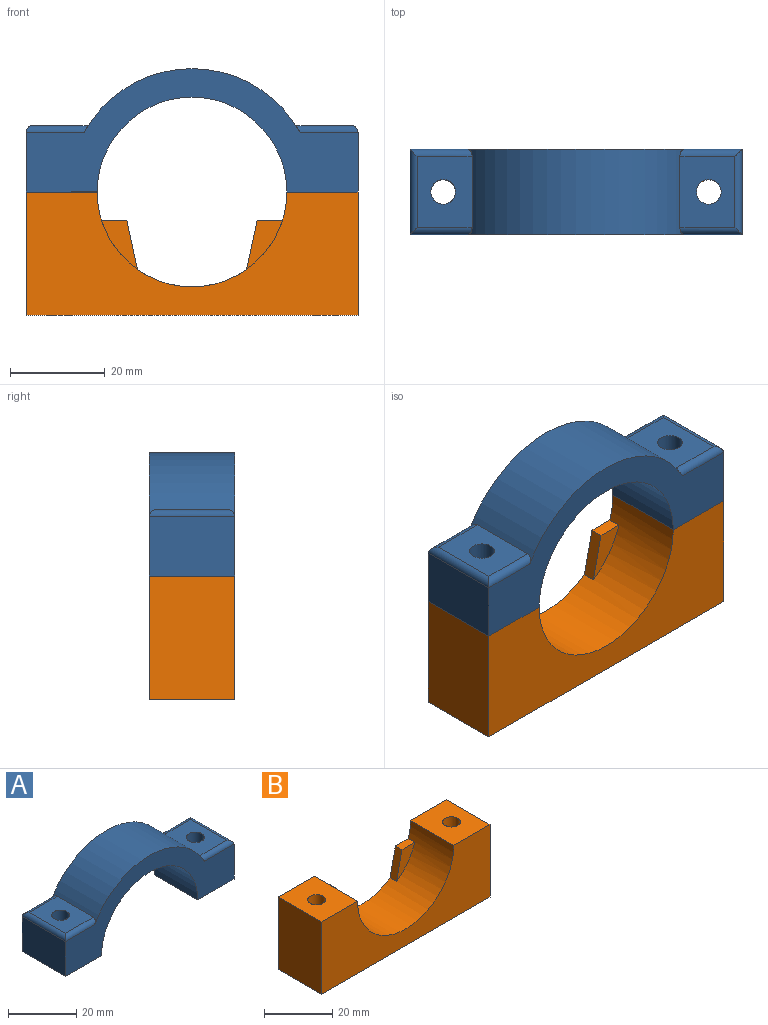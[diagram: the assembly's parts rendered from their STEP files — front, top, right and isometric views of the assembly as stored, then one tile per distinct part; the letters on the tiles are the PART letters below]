
ASSEMBLY  parts=2 mates=1
PART A: 18 faces, bbox 70x18x26 mm
  f0: plane 15x11.59mm, normal (0,0,1), area 152.6mm2, adj f7,f11,f12,f13,f14
  f1: plane 18x12.5mm, normal (-1,0,0), area 225mm2, adj f2,f8,f9,f14
  f2: plane 18x15mm, normal (0,0,-1), area 248.8mm2, adj f1,f3,f8,f9,f11
  f3: cylinder r=20mm len=40mm, axis (0,1,0), area 1131mm2, adj f2,f4,f8,f9
  f4: plane 18x15mm, normal (0,0,-1), area 248.8mm2, adj f3,f5,f8,f9,f10
  f5: plane 18x12.5mm, normal (1,0,0), area 225mm2, adj f4,f8,f9,f17
  f6: plane 15x11.59mm, normal (0,0,1), area 152.6mm2, adj f7,f10,f15,f16,f17
  f7: cylinder r=26mm len=45.6mm, axis (0,1,0), area 940.3mm2, adj f0,f6,f8,f9,f12,f13,f15,f16
  f8: plane 70x26mm, normal (0,-1,0), area 684.5mm2, adj f1,f2,f3,f4,f5,f7,f12,f15
  f9: plane 70x26mm, normal (0,1,0), area 684.5mm2, adj f1,f2,f3,f4,f5,f7,f13,f16
  f10: cylinder r=2.6mm len=14mm, axis (0,0,-1), area 228.7mm2, adj f4,f6
  f11: cylinder r=2.6mm len=14mm, axis (0,0,-1), area 228.7mm2, adj f0,f2
  f12: cylinder r=1.5mm len=13.09mm, axis (1,0,0), area 28.8mm2, adj f0,f7,f8,f14
  f13: cylinder r=1.5mm len=13.09mm, axis (-1,0,0), area 28.8mm2, adj f0,f7,f9,f14
  f14: cylinder r=1.5mm len=18mm, axis (0,-1,0), area 39.8mm2, adj f0,f1,f12,f13
  f15: cylinder r=1.5mm len=13.09mm, axis (1,0,0), area 28.8mm2, adj f6,f7,f8,f17
  f16: cylinder r=1.5mm len=13.09mm, axis (-1,0,0), area 28.8mm2, adj f6,f7,f9,f17
  f17: cylinder r=1.5mm len=18mm, axis (0,1,0), area 39.8mm2, adj f5,f6,f15,f16
PART B: 16 faces, bbox 70x18x26 mm
  f0: cylinder r=20mm len=40mm, axis (0,1,0), area 1060.4mm2, adj f1,f5,f6,f7,f8,f9,f10,f11
  f1: plane 18x15mm, normal (0,0,1), area 248.8mm2, adj f0,f2,f6,f7,f15
  f2: plane 26x18mm, normal (-1,0,0), area 468mm2, adj f1,f3,f6,f7
  f3: plane 70x18mm, normal (0,0,-1), area 1217.5mm2, adj f2,f4,f6,f7,f14,f15
  f4: plane 26x18mm, normal (1,0,0), area 468mm2, adj f3,f5,f6,f7
  f5: plane 18x15mm, normal (0,0,1), area 248.8mm2, adj f0,f4,f6,f7,f14
  f6: plane 70x26mm, normal (0,-1,0), area 1191.7mm2, adj f0,f1,f2,f3,f4,f5
  f7: plane 70x26mm, normal (0,1,0), area 1265.1mm2, adj f0,f1,f2,f3,f4,f5,f8,f9
  f8: plane 10.36x2.7mm, normal (-0.98,0,0.21), area 28.6mm2, adj f0,f7,f9,f10
  f9: plane 5.33x2.7mm, normal (0,0,1), area 14.4mm2, adj f0,f7,f8,f10
  f10: plane 10.36x7.58mm, normal (0,-1,0), area 36.7mm2, adj f0,f8,f9
  f11: plane 10.36x2.7mm, normal (0.98,0,0.21), area 28.6mm2, adj f0,f7,f12,f13
  f12: plane 5.33x2.7mm, normal (0,0,1), area 14.4mm2, adj f0,f7,f11,f13
  f13: plane 10.36x7.58mm, normal (0,-1,0), area 36.7mm2, adj f0,f11,f12
  f14: cylinder r=2.6mm len=26mm, axis (0,0,-1), area 424.7mm2, adj f3,f5
  f15: cylinder r=2.6mm len=26mm, axis (0,0,-1), area 424.7mm2, adj f1,f3
PLACE A t=(31.49,9,21.07)mm
PLACE B t=(31.49,9,21.07)mm
MATE planar B.f5 <-> A.f4  axis (0,0,1) through (66.49,-9,21.07)mm
